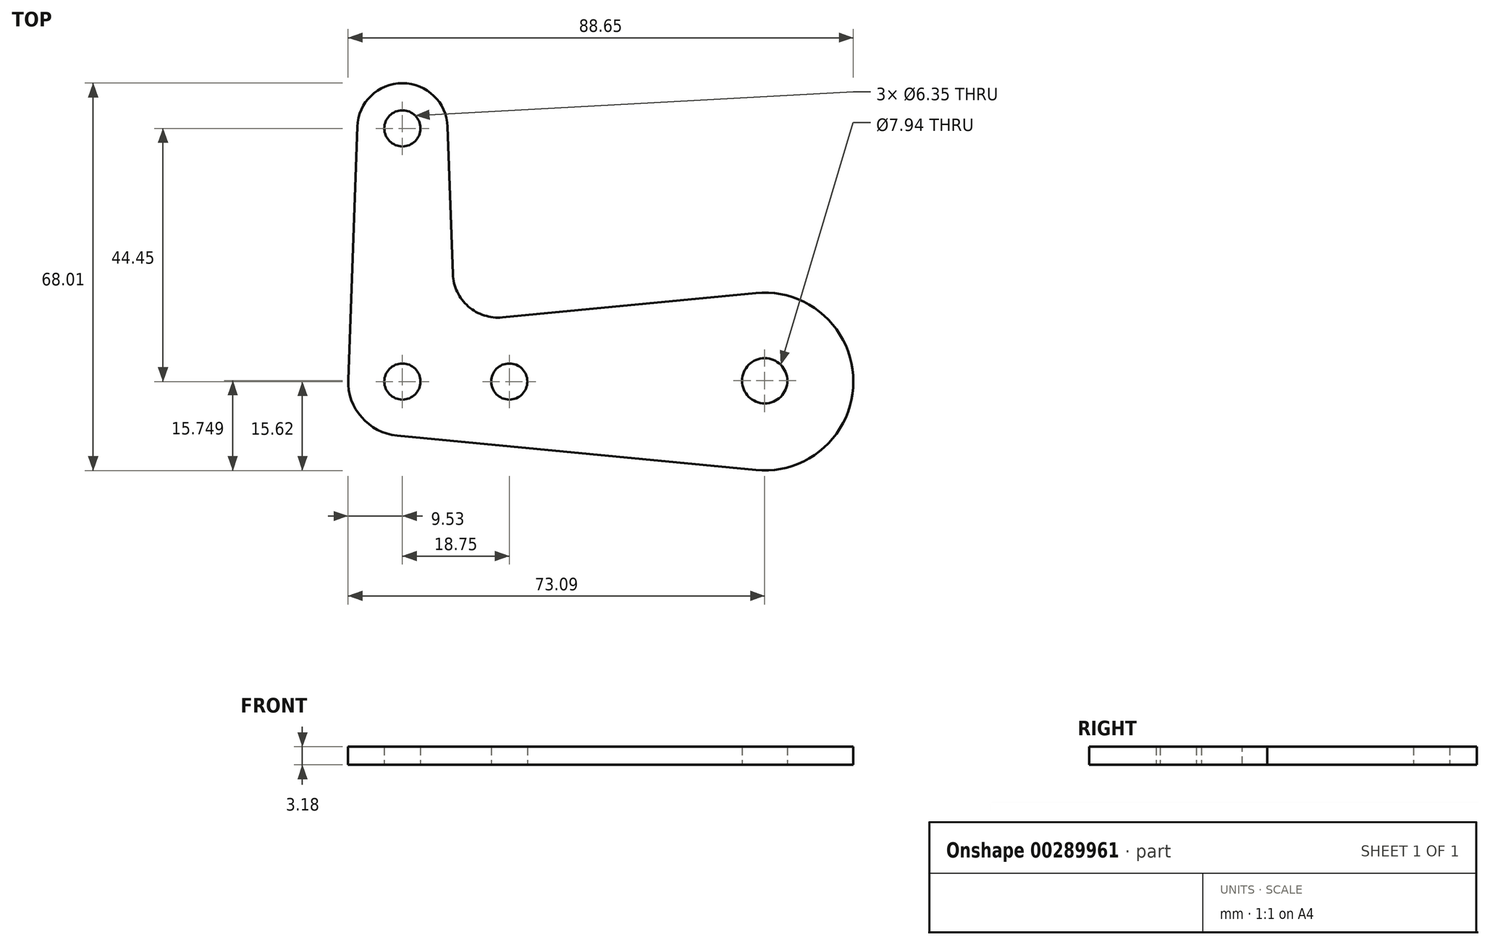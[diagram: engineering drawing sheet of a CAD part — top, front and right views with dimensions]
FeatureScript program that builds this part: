
annotation { "Feature Type Name" : "Feature", "Feature Type Description" : "" }
export const myFeature = defineFeature(function(context is Context, id is Id, definition is map)
    precondition{}
    {
        {
            var Q0;
            Q0=qCreatedBy(makeId("Top.planeOp"),FACE);
            var sketch = newSketch(context, id + "F0", { "sketchPlane" : qUnion([Q0])});
            skLineSegment(sketch, "E0", {"start": v(0, 0) * mm, "end": v(63.5, 0) * mm, "construction": true});
            skLineSegment(sketch, "E1", {"start": v(0, 0) * mm, "end": v(0, 44.45) * mm, "construction": true});
            skLineSegment(sketch, "E2", {"start": v(0, 44.45) * mm, "end": v(0, 158.06) * mm, "construction": true});
            skLineSegment(sketch, "E3", {"start": v(63.5, 0) * mm, "end": v(274.96, 0) * mm, "construction": true});
            skCircle(sketch, "E4", {"center": v(0, 0) * mm, "radius": 9.53 * mm});
            skCircle(sketch, "E5", {"center": v(63.5, 0) * mm, "radius": 15.62 * mm});
            skCircle(sketch, "E6", {"center": v(63.56, 0.13) * mm, "radius": 3.97 * mm});
            skCircle(sketch, "E7", {"center": v(0, 0) * mm, "radius": 3.18 * mm});
            skCircle(sketch, "E8", {"center": v(0, 44.45) * mm, "radius": 7.94 * mm});
            skCircle(sketch, "E9", {"center": v(0, 44.45) * mm, "radius": 3.18 * mm});
            skCircle(sketch, "E10", {"center": v(18.75, 0) * mm, "radius": 3.18 * mm});
            skLineSegment(sketch, "E11", {"start": v(62, 15.55) * mm, "end": v(-0.91, 9.48) * mm});
            skLineSegment(sketch, "E12", {"start": v(62, -15.55) * mm, "end": v(-0.91, -9.48) * mm});
            skLineSegment(sketch, "E13", {"start": v(9.53, 0) * mm, "end": v(7.93, 44.73) * mm});
            skLineSegment(sketch, "E14", {"start": v(-7.93, 44.73) * mm, "end": v(-9.52, 0.34) * mm});
            skPoint(sketch, "E15.orphan", {"position": v(7.24, 64.1) * mm});
            skPoint(sketch, "E16.orphan", {"position": v(-7.24, 64.1) * mm});
            skSolve(sketch);
        }
        {
            var Q0;
            Q0=qSketchRegion(id+"F0",true);
            extrude(context, id + "F1", {"entities" : qUnion([Q0]), "depth" : 3.17 * mm});
        }
        {
            var Q0;
            Q0=makeQuery(id+"F1.opExtrude","SWEPT_EDGE",EDGE,{"disambiguationData":[OSD([sQuery(id+"F0.wireOp",EDGE,"E11"),sQuery(id+"F0.wireOp",EDGE,"E13")])]});
            fillet(context, id + "F2", {"entities" : qUnion([Q0]), "radius" : 7.94 * mm, "tangentPropagation" : true, "allowEdgeOverflow" : false});
        }
    });
